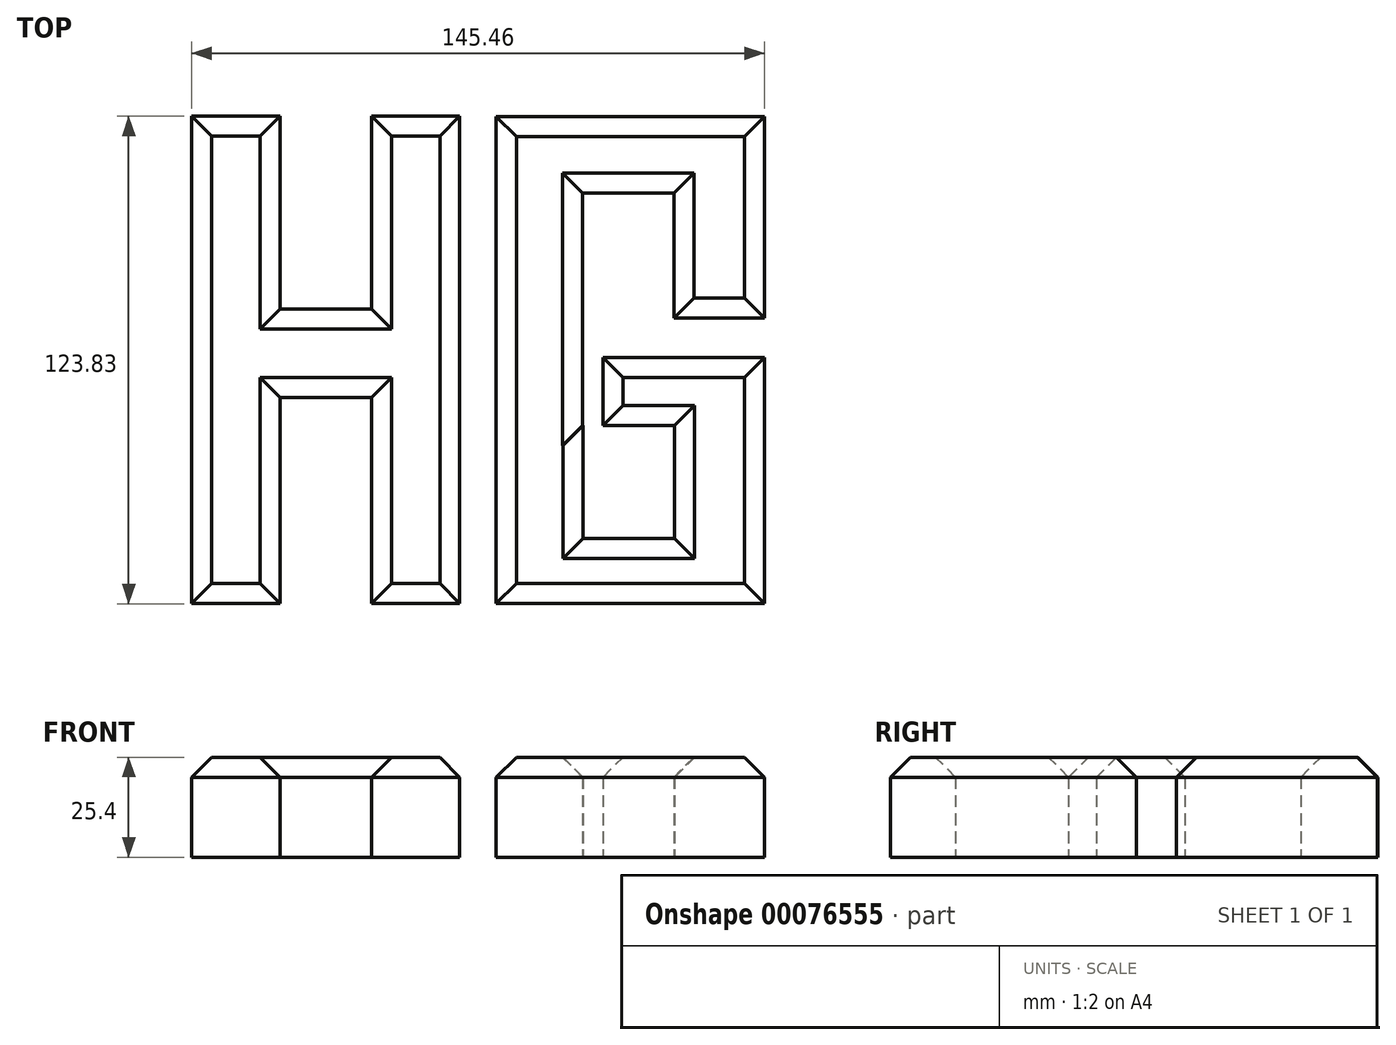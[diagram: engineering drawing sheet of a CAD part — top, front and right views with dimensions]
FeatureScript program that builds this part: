
annotation { "Feature Type Name" : "Feature", "Feature Type Description" : "" }
export const myFeature = defineFeature(function(context is Context, id is Id, definition is map)
    precondition{}
    {
        {
            var Q0;
            Q0=qCreatedBy(makeId("Top.planeOp"),FACE);
            var sketch = newSketch(context, id + "F0", { "sketchPlane" : qUnion([Q0])});
            skLineSegment(sketch, "E0.bottom", {"start": v(-73.08, 61.24) * mm, "end": v(-4.98, 61.24) * mm});
            skLineSegment(sketch, "E0.top", {"start": v(-73.08, -62.49) * mm, "end": v(-4.98, -62.49) * mm});
            skLineSegment(sketch, "E0.left", {"start": v(-73.08, 61.24) * mm, "end": v(-73.08, -62.49) * mm});
            skLineSegment(sketch, "E0.right", {"start": v(-4.98, 61.24) * mm, "end": v(-4.98, -62.49) * mm});
            skLineSegment(sketch, "E1.bottom", {"start": v(-50.65, 61.24) * mm, "end": v(-27.4, 61.24) * mm});
            skLineSegment(sketch, "E1.top", {"start": v(-50.65, 12.25) * mm, "end": v(-27.4, 12.25) * mm});
            skLineSegment(sketch, "E1.left", {"start": v(-50.65, 61.24) * mm, "end": v(-50.65, 12.25) * mm});
            skLineSegment(sketch, "E1.right", {"start": v(-27.4, 61.24) * mm, "end": v(-27.4, 12.25) * mm});
            skLineSegment(sketch, "E2.bottom", {"start": v(-50.65, -10.17) * mm, "end": v(-27.4, -10.17) * mm});
            skLineSegment(sketch, "E2.top", {"start": v(-50.65, -62.49) * mm, "end": v(-27.4, -62.49) * mm});
            skLineSegment(sketch, "E2.left", {"start": v(-50.65, -10.17) * mm, "end": v(-50.65, -62.49) * mm});
            skLineSegment(sketch, "E2.right", {"start": v(-27.4, -10.17) * mm, "end": v(-27.4, -62.49) * mm});
            skLineSegment(sketch, "E3.bottom", {"start": v(4.29, 61.14) * mm, "end": v(72.38, 61.14) * mm});
            skLineSegment(sketch, "E3.top", {"start": v(4.29, -62.59) * mm, "end": v(72.38, -62.59) * mm});
            skLineSegment(sketch, "E3.left", {"start": v(4.29, 61.14) * mm, "end": v(4.29, -62.59) * mm});
            skLineSegment(sketch, "E3.right", {"start": v(72.38, 61.14) * mm, "end": v(72.38, -62.59) * mm});
            skLineSegment(sketch, "E4.bottom", {"start": v(26.2, 41.68) * mm, "end": v(49.46, 41.68) * mm});
            skLineSegment(sketch, "E4.top", {"start": v(26.2, 0) * mm, "end": v(49.46, 0) * mm});
            skLineSegment(sketch, "E4.left", {"start": v(26.2, 41.68) * mm, "end": v(26.2, 0) * mm});
            skLineSegment(sketch, "E4.right", {"start": v(49.46, 41.68) * mm, "end": v(49.46, 0) * mm});
            skLineSegment(sketch, "E5.bottom", {"start": v(26.27, -17.28) * mm, "end": v(49.59, -17.28) * mm});
            skLineSegment(sketch, "E5.top", {"start": v(26.27, -45.97) * mm, "end": v(49.59, -45.97) * mm});
            skLineSegment(sketch, "E5.left", {"start": v(26.27, -17.28) * mm, "end": v(26.27, -45.97) * mm});
            skLineSegment(sketch, "E5.right", {"start": v(49.59, -17.28) * mm, "end": v(49.59, -45.97) * mm});
            skLineSegment(sketch, "E6.bottom", {"start": v(26.2, 0) * mm, "end": v(31.36, 0) * mm});
            skLineSegment(sketch, "E6.top", {"start": v(26.2, -17.28) * mm, "end": v(31.36, -17.28) * mm});
            skLineSegment(sketch, "E6.left", {"start": v(26.2, 0) * mm, "end": v(26.2, -17.28) * mm});
            skLineSegment(sketch, "E6.right", {"start": v(31.36, 0) * mm, "end": v(31.36, -17.28) * mm});
            skLineSegment(sketch, "E7.bottom", {"start": v(72.38, 0) * mm, "end": v(49.46, 0) * mm});
            skLineSegment(sketch, "E7.top", {"start": v(72.38, 10.05) * mm, "end": v(49.46, 10.05) * mm});
            skLineSegment(sketch, "E7.left", {"start": v(72.38, 0) * mm, "end": v(72.38, 10.05) * mm});
            skLineSegment(sketch, "E7.right", {"start": v(49.46, 0) * mm, "end": v(49.46, 10.05) * mm});
            skSolve(sketch);
        }
        {
            var Q0;
            {var subQ0=sQuery(id+"F0.wireOp",EDGE,"E0.left");Q0=makeQuery(id+"F0.imprint","IMPRINT",FACE,{"disambiguationData":[TD([[makeQuery(id+"F0.imprint","IMPRINT",EDGE,{"derivedFrom":subQ0}),1.0]])]});}
            extrude(context, id + "F1", {"entities" : qUnion([Q0]), "depth" : 25.4 * mm});
        }
        {
            var Q0;
            {var subQ3=sQuery(id+"F0.wireOp",EDGE,"E3.bottom");Q0=makeQuery(id+"F0.imprint","IMPRINT",FACE,{"disambiguationData":[TD([[makeQuery(id+"F0.imprint","IMPRINT",EDGE,{"derivedFrom":subQ3}),-1.0]])]});}
            extrude(context, id + "F2", {"entities" : qUnion([Q0]), "depth" : 25.4 * mm});
        }
        {
            var Q0;
            Q0=makeQuery(id+"F1.opExtrude","CAP_FACE",FACE,{"disambiguationData":[OSD([sQuery(id+"F0.wireOp",EDGE,"E0.bottom"),sQuery(id+"F0.wireOp",EDGE,"E0.top"),sQuery(id+"F0.wireOp",EDGE,"E0.left"),sQuery(id+"F0.wireOp",EDGE,"E0.right"),sQuery(id+"F0.wireOp",EDGE,"E1.top"),sQuery(id+"F0.wireOp",EDGE,"E1.left"),sQuery(id+"F0.wireOp",EDGE,"E1.right"),sQuery(id+"F0.wireOp",EDGE,"E2.bottom"),sQuery(id+"F0.wireOp",EDGE,"E2.left"),sQuery(id+"F0.wireOp",EDGE,"E2.right")])],"isStart":false});
            var Q1;
            Q1=makeQuery(id+"F2.opExtrude","CAP_FACE",FACE,{"disambiguationData":[OSD([sQuery(id+"F0.wireOp",EDGE,"E3.bottom"),sQuery(id+"F0.wireOp",EDGE,"E3.top"),sQuery(id+"F0.wireOp",EDGE,"E3.left"),sQuery(id+"F0.wireOp",EDGE,"E3.right"),sQuery(id+"F0.wireOp",EDGE,"E4.bottom"),sQuery(id+"F0.wireOp",EDGE,"E4.top"),sQuery(id+"F0.wireOp",EDGE,"E4.left"),sQuery(id+"F0.wireOp",EDGE,"E4.right"),sQuery(id+"F0.wireOp",EDGE,"E5.bottom"),sQuery(id+"F0.wireOp",EDGE,"E5.top"),sQuery(id+"F0.wireOp",EDGE,"E5.left"),sQuery(id+"F0.wireOp",EDGE,"E5.right"),sQuery(id+"F0.wireOp",EDGE,"E6.top"),sQuery(id+"F0.wireOp",EDGE,"E6.left"),sQuery(id+"F0.wireOp",EDGE,"E6.right"),sQuery(id+"F0.wireOp",EDGE,"E7.bottom"),sQuery(id+"F0.wireOp",EDGE,"E7.top")])],"isStart":false});
            chamfer(context, id + "F3", {"entities" : qUnion([Q0, Q1]), "width" : 5.08 * mm, "tangentPropagation" : true});
        }
    });
